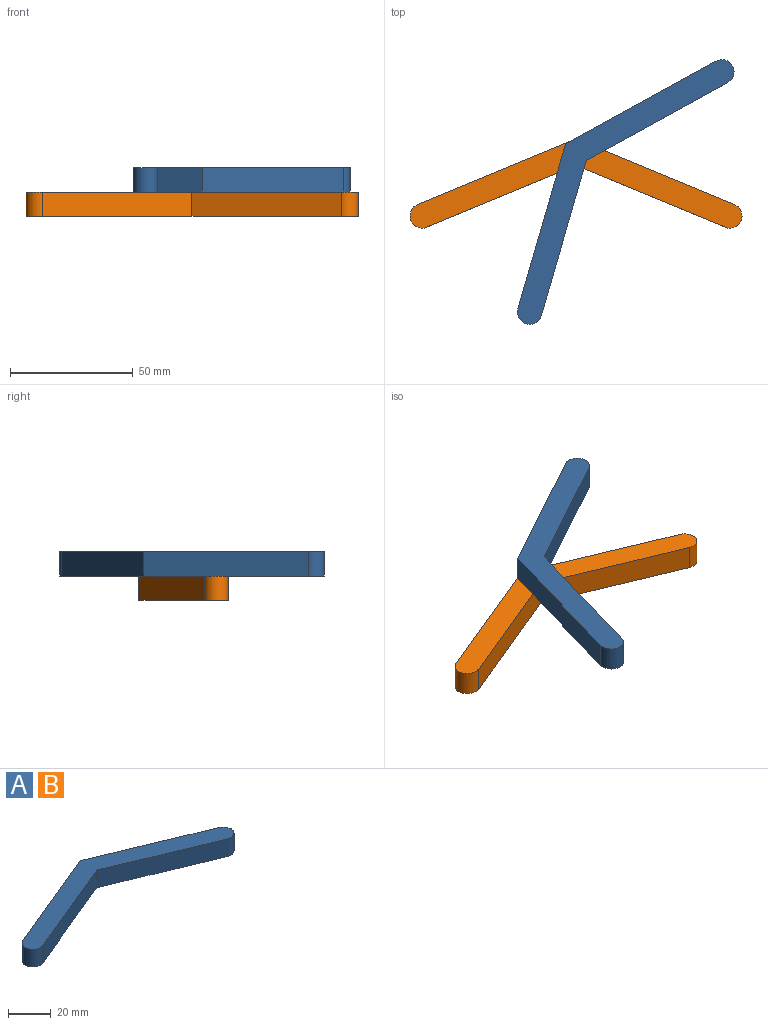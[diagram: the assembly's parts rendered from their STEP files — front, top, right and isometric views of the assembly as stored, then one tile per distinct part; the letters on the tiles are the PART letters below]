
ASSEMBLY  parts=2 mates=1
PART A: 8 faces, bbox 135.5x36.4x10 mm
  f0: cylinder r=5mm len=10mm, axis (0,0,-1), area 157.1mm2, adj f1,f5,f6,f7
  f1: plane 64.67x26.79mm, normal (0.38,0.92,0), area 700mm2, adj f0,f2,f6,f7
  f2: plane 64.67x26.79mm, normal (-0.38,0.92,0), area 700mm2, adj f1,f3,f6,f7
  f3: cylinder r=5mm len=10mm, axis (0,0,-1), area 157.1mm2, adj f2,f4,f6,f7
  f4: plane 60.84x25.2mm, normal (0.38,-0.92,0), area 658.6mm2, adj f3,f5,f6,f7
  f5: plane 60.84x25.2mm, normal (-0.38,-0.92,0), area 658.6mm2, adj f0,f4,f6,f7
  f6: plane 135.52x36.41mm, normal (0,0,1), area 1437.1mm2, adj f0,f1,f2,f3,f4,f5
  f7: plane 135.52x36.41mm, normal (0,0,-1), area 1437.1mm2, adj f0,f1,f2,f3,f4,f5
PART B: same geometry as A
PLACE A rot(axis=(0,0,1),51.3deg) t=(-5.49,13.53,6.41)mm
PLACE B t=(-9.71,11.5,-3.59)mm fixed
MATE revolute A.f7 <-> B.f6  axis (0,0,-1) through (-9.71,16.92,6.41)mm
